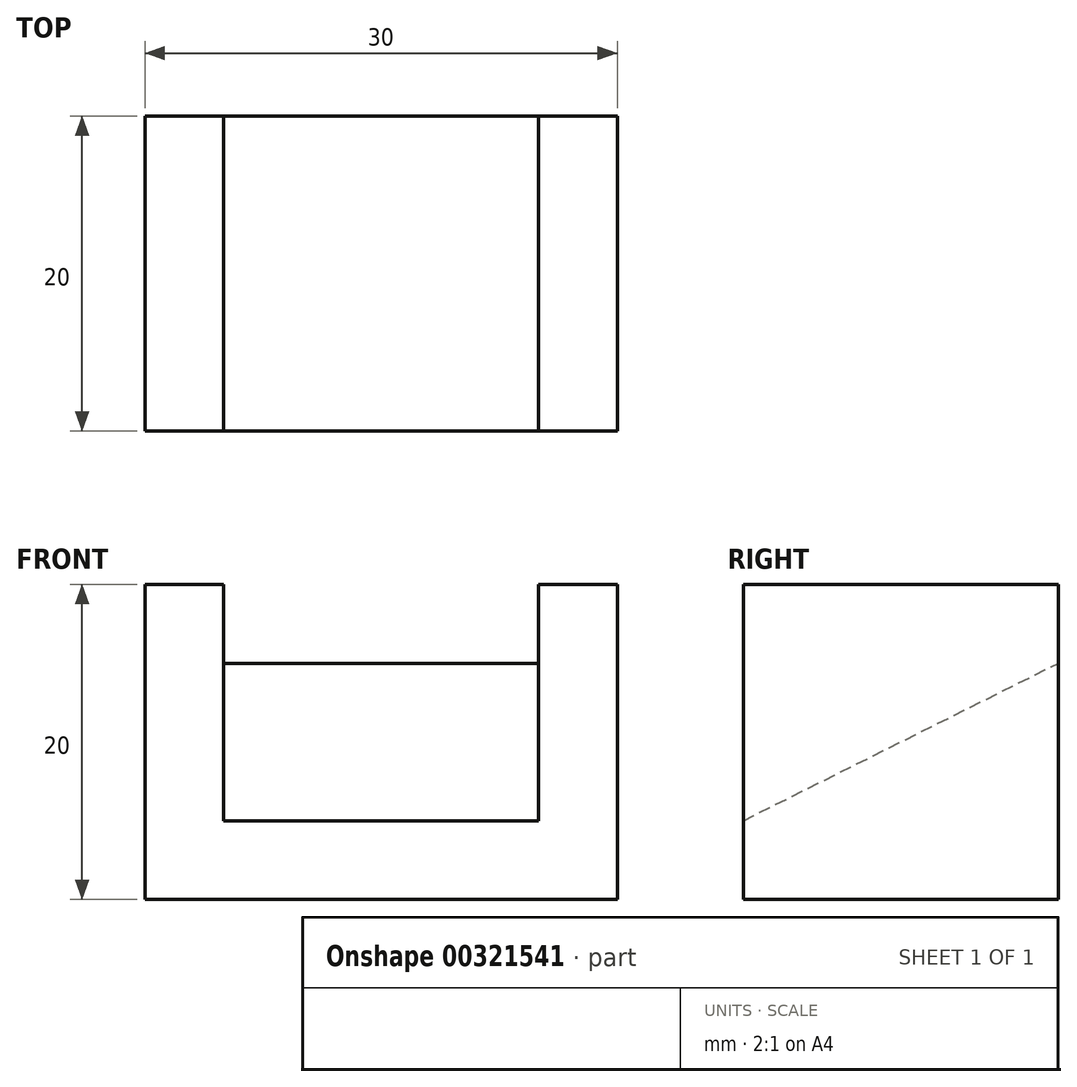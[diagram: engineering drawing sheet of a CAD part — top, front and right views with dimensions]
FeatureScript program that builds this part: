
annotation { "Feature Type Name" : "Feature", "Feature Type Description" : "" }
export const myFeature = defineFeature(function(context is Context, id is Id, definition is map)
    precondition{}
    {
        {
            var Q0;
            Q0=qCreatedBy(makeId("Front.planeOp"),FACE);
            var sketch = newSketch(context, id + "F0", { "sketchPlane" : qUnion([Q0])});
            skLineSegment(sketch, "E0", {"start": v(0, 0) * mm, "end": v(0, 20) * mm});
            skLineSegment(sketch, "E1", {"start": v(0, 20) * mm, "end": v(5, 20) * mm});
            skLineSegment(sketch, "E2", {"start": v(5, 20) * mm, "end": v(5, 5) * mm});
            skLineSegment(sketch, "E3", {"start": v(5, 5) * mm, "end": v(25, 5) * mm});
            skLineSegment(sketch, "E4", {"start": v(25, 5) * mm, "end": v(25, 20) * mm});
            skLineSegment(sketch, "E5", {"start": v(25, 20) * mm, "end": v(30, 20) * mm});
            skLineSegment(sketch, "E6", {"start": v(30, 20) * mm, "end": v(30, 0) * mm});
            skLineSegment(sketch, "E7", {"start": v(30, 0) * mm, "end": v(0, 0) * mm});
            skSolve(sketch);
        }
        {
            var Q0;
            Q0=makeQuery(id+"F0.imprint","IMPRINT",FACE,{"disambiguationData":[TD([[makeQuery(id+"F0.imprint","IMPRINT",EDGE,{"derivedFrom":sQuery(id+"F0.wireOp",EDGE,"E0")}),-1.0]])]});
            extrude(context, id + "F1", {"entities" : qUnion([Q0]), "depth" : 20 * mm});
        }
        {
            var Q0;
            Q0=makeQuery(id+"F1.opExtrude","SWEPT_FACE",FACE,{"disambiguationData":[OSD([sQuery(id+"F0.wireOp",EDGE,"E6")])]});
            var sketch = newSketch(context, id + "F2", { "sketchPlane" : qUnion([Q0])});
            skLineSegment(sketch, "E8", {"start": v(0, 15) * mm, "end": v(-20, 5) * mm});
            skLineSegment(sketch, "E9", {"start": v(-20, 5) * mm, "end": v(0, 5) * mm});
            skLineSegment(sketch, "E10", {"start": v(0, 5) * mm, "end": v(0, 15) * mm});
            skSolve(sketch);
        }
        {
            var Q0;
            Q0=makeQuery(id+"F2.imprint","IMPRINT",FACE,{"disambiguationData":[TD([[makeQuery(id+"F2.imprint","IMPRINT",EDGE,{"derivedFrom":sQuery(id+"F2.wireOp",EDGE,"E8")}),1.0]])]});
            extrude(context, id + "F3", {"entities" : qUnion([Q0]), "operationType" : NewBodyOperationType.ADD, "oppositeDirection" : true, "depth" : 30 * mm});
        }
    });
